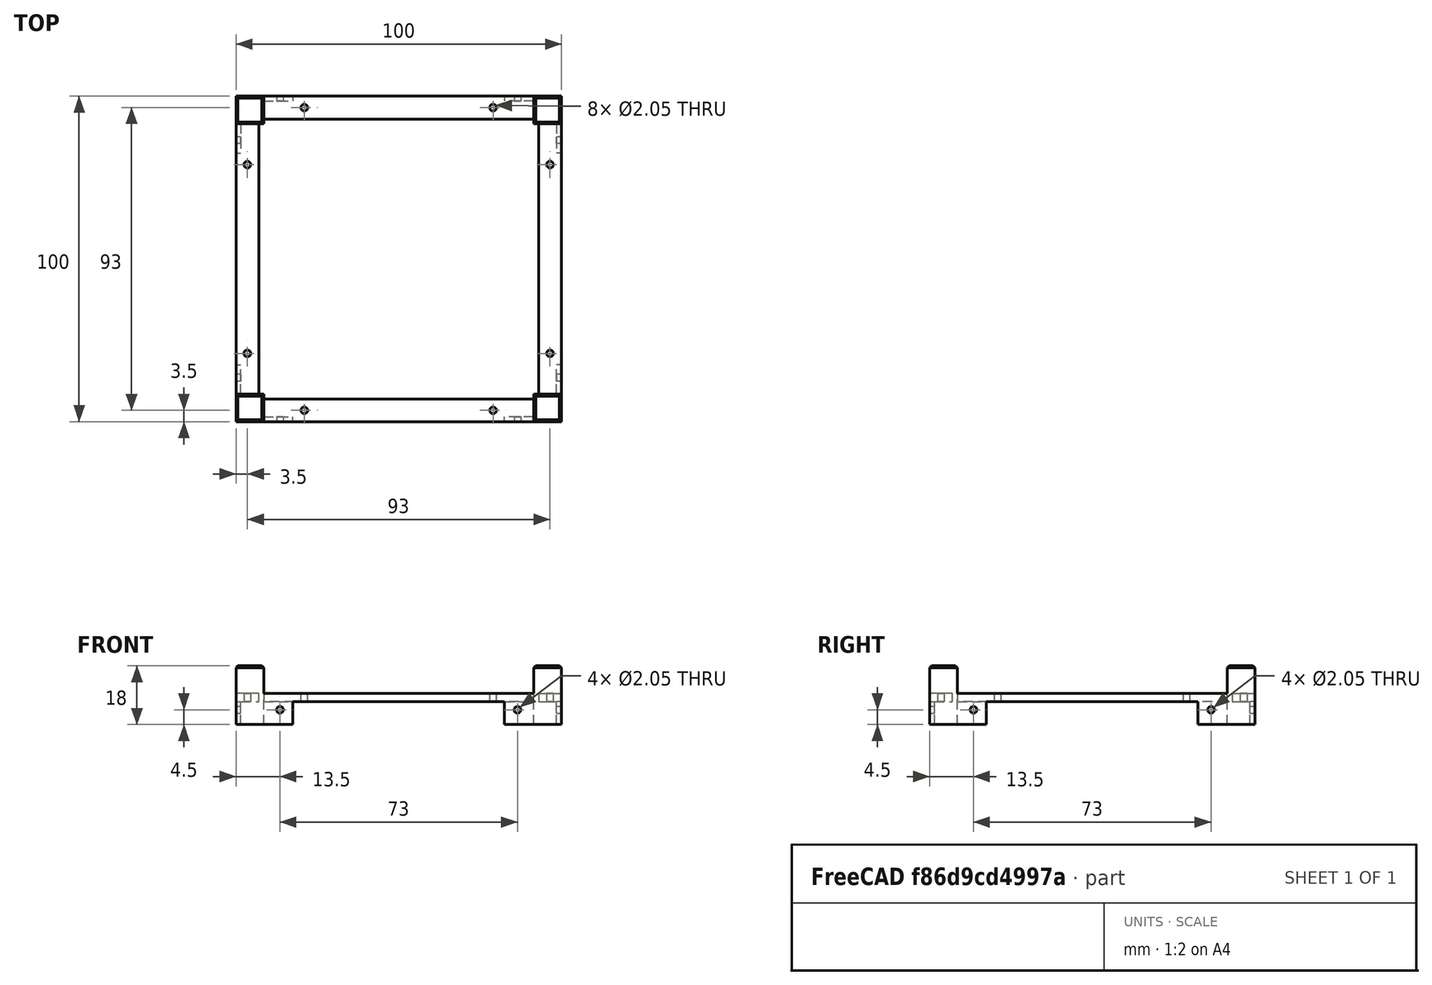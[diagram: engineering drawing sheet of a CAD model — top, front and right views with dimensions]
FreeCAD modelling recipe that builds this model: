
FCSTD DOCUMENT  (FreeCAD 0.20R29603 (Git))
Label: OpenSCAD_MyChassisModeling
License: All rights reserved
LicenseURL: http://en.wikipedia.org/wiki/All_rights_reserved
objects: Part::Box×72, Part::Fuse×56, Part::Cylinder×32, Part::Cut×17, Part::MultiFuse×13, Part::Mirroring×8, TechDraw::DrawViewDimension×5, TechDraw::DrawViewPart×3, Part::FeaturePython×1, TechDraw::DrawSVGTemplate×1, TechDraw::DrawViewAnnotation×1, TechDraw::DrawPage×1
note: 199 computed .brp shape members not serialized (recipe doc carries the construction recipe); baked Part::Feature solids carry a one-line shape summary decoded from their .brp

FEATURE [Part::Box] cube
  AttacherType = Attacher::AttachEngine3D
  Height = 2.5
  Length = 100
  Placement = pos=(-50,-3.5,-2.5) rot=(0,0,1;0rad)
  Width = 7
FEATURE [Part::Cylinder] cylinder
  Angle = 360
  AttacherType = Attacher::AttachEngine3D
  FirstAngle = 0
  Height = 100
  Placement = pos=(-29,0,-50) rot=(0,0,1;0rad)
  Radius = 1.025
  SecondAngle = 0
FEATURE [Part::Cylinder] cylinder001
  Angle = 360
  AttacherType = Attacher::AttachEngine3D
  FirstAngle = 0
  Height = 100
  Placement = pos=(29,0,-50) rot=(0,0,1;0rad)
  Radius = 1.025
  SecondAngle = 0
FEATURE [Part::Fuse] Group
  Base = -> cylinder
  Tool = -> cylinder001
FEATURE [Part::Cut] difference
  Base = -> cube
  Placement = pos=(0,46.5,0) rot=(0,0,1;0rad)
  Tool = -> Group
FEATURE [Part::Box] cube001
  AttacherType = Attacher::AttachEngine3D
  Height = 2.5
  Length = 100
  Placement = pos=(-50,-3.5,-2.5) rot=(0,0,1;0rad)
  Width = 7
FEATURE [Part::Cylinder] cylinder002
  Angle = 360
  AttacherType = Attacher::AttachEngine3D
  FirstAngle = 0
  Height = 100
  Placement = pos=(-29,0,-50) rot=(0,0,1;0rad)
  Radius = 1.025
  SecondAngle = 0
FEATURE [Part::Cylinder] cylinder003
  Angle = 360
  AttacherType = Attacher::AttachEngine3D
  FirstAngle = 0
  Height = 100
  Placement = pos=(29,0,-50) rot=(0,0,1;0rad)
  Radius = 1.025
  SecondAngle = 0
FEATURE [Part::Fuse] Group001
  Base = -> cylinder002
  Tool = -> cylinder003
FEATURE [Part::Cut] difference001
  Base = -> cube001
  Placement = pos=(0,46.5,0) rot=(0,0,1;0rad)
  Tool = -> Group001
FEATURE [Part::Fuse] Group002
  Base = -> difference
  Tool = -> difference001
FEATURE [Part::Box] cube002
  AttacherType = Attacher::AttachEngine3D
  Height = 2.5
  Length = 100
  Placement = pos=(-50,-3.5,-2.5) rot=(0,0,1;0rad)
  Width = 7
FEATURE [Part::Cylinder] cylinder004
  Angle = 360
  AttacherType = Attacher::AttachEngine3D
  FirstAngle = 0
  Height = 100
  Placement = pos=(-29,0,-50) rot=(0,0,1;0rad)
  Radius = 1.025
  SecondAngle = 0
FEATURE [Part::Cylinder] cylinder005
  Angle = 360
  AttacherType = Attacher::AttachEngine3D
  FirstAngle = 0
  Height = 100
  Placement = pos=(29,0,-50) rot=(0,0,1;0rad)
  Radius = 1.025
  SecondAngle = 0
FEATURE [Part::Fuse] Group003
  Base = -> cylinder004
  Tool = -> cylinder005
FEATURE [Part::Cut] difference002
  Base = -> cube002
  Placement = pos=(0,46.5,0) rot=(0,0,1;0rad)
  Tool = -> Group003
FEATURE [Part::Box] cube003
  AttacherType = Attacher::AttachEngine3D
  Height = 2.5
  Length = 100
  Placement = pos=(-50,-3.5,-2.5) rot=(0,0,1;0rad)
  Width = 7
FEATURE [Part::Cylinder] cylinder006
  Angle = 360
  AttacherType = Attacher::AttachEngine3D
  FirstAngle = 0
  Height = 100
  Placement = pos=(-29,0,-50) rot=(0,0,1;0rad)
  Radius = 1.025
  SecondAngle = 0
FEATURE [Part::Cylinder] cylinder007
  Angle = 360
  AttacherType = Attacher::AttachEngine3D
  FirstAngle = 0
  Height = 100
  Placement = pos=(29,0,-50) rot=(0,0,1;0rad)
  Radius = 1.025
  SecondAngle = 0
FEATURE [Part::Fuse] Group004
  Base = -> cylinder006
  Tool = -> cylinder007
FEATURE [Part::Cut] difference003
  Base = -> cube003
  Placement = pos=(-46.5,0,0) rot=(0,0,1;1.5708rad)
  Tool = -> Group004
FEATURE [Part::Fuse] Group005
  Base = -> difference002
  Tool = -> difference003
FEATURE [Part::Box] cube004
  AttacherType = Attacher::AttachEngine3D
  Height = 2.5
  Length = 100
  Placement = pos=(-50,-3.5,-2.5) rot=(0,0,1;0rad)
  Width = 7
FEATURE [Part::Cylinder] cylinder008
  Angle = 360
  AttacherType = Attacher::AttachEngine3D
  FirstAngle = 0
  Height = 100
  Placement = pos=(-29,0,-50) rot=(0,0,1;0rad)
  Radius = 1.025
  SecondAngle = 0
FEATURE [Part::Cylinder] cylinder009
  Angle = 360
  AttacherType = Attacher::AttachEngine3D
  FirstAngle = 0
  Height = 100
  Placement = pos=(29,0,-50) rot=(0,0,1;0rad)
  Radius = 1.025
  SecondAngle = 0
FEATURE [Part::Fuse] Group006
  Base = -> cylinder008
  Tool = -> cylinder009
FEATURE [Part::Cut] difference004
  Base = -> cube004
  Placement = pos=(0,46.5,0) rot=(0,0,1;0rad)
  Tool = -> Group006
FEATURE [Part::Box] cube005
  AttacherType = Attacher::AttachEngine3D
  Height = 2.5
  Length = 100
  Placement = pos=(-50,-3.5,-2.5) rot=(0,0,1;0rad)
  Width = 7
FEATURE [Part::Cylinder] cylinder010
  Angle = 360
  AttacherType = Attacher::AttachEngine3D
  FirstAngle = 0
  Height = 100
  Placement = pos=(-29,0,-50) rot=(0,0,1;0rad)
  Radius = 1.025
  SecondAngle = 0
FEATURE [Part::Cylinder] cylinder011
  Angle = 360
  AttacherType = Attacher::AttachEngine3D
  FirstAngle = 0
  Height = 100
  Placement = pos=(29,0,-50) rot=(0,0,1;0rad)
  Radius = 1.025
  SecondAngle = 0
FEATURE [Part::Fuse] Group007
  Base = -> cylinder010
  Tool = -> cylinder011
FEATURE [Part::Cut] difference005
  Base = -> cube005
  Placement = pos=(-5.7e-15,-46.5,0) rot=(0,0,1;3.14159rad)
  Tool = -> Group007
FEATURE [Part::Fuse] Group008
  Base = -> difference004
  Tool = -> difference005
FEATURE [Part::Box] cube006
  AttacherType = Attacher::AttachEngine3D
  Height = 2.5
  Length = 100
  Placement = pos=(-50,-3.5,-2.5) rot=(0,0,1;0rad)
  Width = 7
FEATURE [Part::Cylinder] cylinder012
  Angle = 360
  AttacherType = Attacher::AttachEngine3D
  FirstAngle = 0
  Height = 100
  Placement = pos=(-29,0,-50) rot=(0,0,1;0rad)
  Radius = 1.025
  SecondAngle = 0
FEATURE [Part::Cylinder] cylinder013
  Angle = 360
  AttacherType = Attacher::AttachEngine3D
  FirstAngle = 0
  Height = 100
  Placement = pos=(29,0,-50) rot=(0,0,1;0rad)
  Radius = 1.025
  SecondAngle = 0
FEATURE [Part::Fuse] Group009
  Base = -> cylinder012
  Tool = -> cylinder013
FEATURE [Part::Cut] difference006
  Base = -> cube006
  Placement = pos=(0,46.5,0) rot=(0,0,1;0rad)
  Tool = -> Group009
FEATURE [Part::Box] cube007
  AttacherType = Attacher::AttachEngine3D
  Height = 2.5
  Length = 100
  Placement = pos=(-50,-3.5,-2.5) rot=(0,0,1;0rad)
  Width = 7
FEATURE [Part::Cylinder] cylinder014
  Angle = 360
  AttacherType = Attacher::AttachEngine3D
  FirstAngle = 0
  Height = 100
  Placement = pos=(-29,0,-50) rot=(0,0,1;0rad)
  Radius = 1.025
  SecondAngle = 0
FEATURE [Part::Cylinder] cylinder015
  Angle = 360
  AttacherType = Attacher::AttachEngine3D
  FirstAngle = 0
  Height = 100
  Placement = pos=(29,0,-50) rot=(0,0,1;0rad)
  Radius = 1.025
  SecondAngle = 0
FEATURE [Part::Fuse] Group010
  Base = -> cylinder014
  Tool = -> cylinder015
FEATURE [Part::Cut] difference007
  Base = -> cube007
  Placement = pos=(46.5,0,0) rot=(0,0,-1;1.5708rad)
  Tool = -> Group010
FEATURE [Part::Fuse] Group011
  Base = -> difference006
  Tool = -> difference007
FEATURE [Part::MultiFuse] Group012
  Shapes = -> [Group002,Group005,Group008,Group011]
FEATURE [Part::Box] cube008
  AttacherType = Attacher::AttachEngine3D
  Height = 18
  Length = 8.5
  Placement = pos=(-4.25,-4.25,-18) rot=(0,0,1;0rad)
  Width = 8.5
FEATURE [Part::Box] cube009
  AttacherType = Attacher::AttachEngine3D
  Height = 100
  Length = 9.5
  Placement = pos=(-4.75,42.3466,-38.7141) rot=(1,0,0;0.785398rad)
  Width = 9.5
FEATURE [Part::Box] cube010
  AttacherType = Attacher::AttachEngine3D
  Height = 100
  Length = 9.5
  Placement = pos=(-42.3466,-4.75,-38.7141) rot=(0.357407,0.357407,0.862856;1.71777rad)
  Width = 9.5
FEATURE [Part::Fuse] Group013
  Base = -> cube009
  Tool = -> cube010
FEATURE [Part::Box] cube011
  AttacherType = Attacher::AttachEngine3D
  Height = 100
  Length = 9.5
  Placement = pos=(-4.75,42.3466,-38.7141) rot=(1,0,0;0.785398rad)
  Width = 9.5
FEATURE [Part::Box] cube012
  AttacherType = Attacher::AttachEngine3D
  Height = 100
  Length = 9.5
  Placement = pos=(4.75,-42.3466,-38.7141) rot=(0,0.382683,0.92388;3.14159rad)
  Width = 9.5
FEATURE [Part::Fuse] Group014
  Base = -> cube011
  Tool = -> cube012
FEATURE [Part::Box] cube013
  AttacherType = Attacher::AttachEngine3D
  Height = 100
  Length = 9.5
  Placement = pos=(-4.75,42.3466,-38.7141) rot=(1,0,0;0.785398rad)
  Width = 9.5
FEATURE [Part::Box] cube014
  AttacherType = Attacher::AttachEngine3D
  Height = 100
  Length = 9.5
  Placement = pos=(42.3466,4.75,-38.7141) rot=(0.357407,-0.357407,-0.862856;1.71777rad)
  Width = 9.5
FEATURE [Part::Fuse] Group015
  Base = -> cube013
  Tool = -> cube014
FEATURE [Part::MultiFuse] Group016
  Shapes = -> [Group013,Group014,Group015]
FEATURE [Part::Cut] difference008
  Base = -> cube008
  Placement = pos=(-45.75,-45.75,8.5) rot=(0,0,1;0rad)
  Tool = -> Group016
FEATURE [Part::Box] cube015
  AttacherType = Attacher::AttachEngine3D
  Height = 18
  Length = 8.5
  Placement = pos=(-4.25,-4.25,-18) rot=(0,0,1;0rad)
  Width = 8.5
FEATURE [Part::Box] cube016
  AttacherType = Attacher::AttachEngine3D
  Height = 100
  Length = 9.5
  Placement = pos=(-4.75,42.3466,-38.7141) rot=(1,0,0;0.785398rad)
  Width = 9.5
FEATURE [Part::Box] cube017
  AttacherType = Attacher::AttachEngine3D
  Height = 100
  Length = 9.5
  Placement = pos=(-42.3466,-4.75,-38.7141) rot=(0.357407,0.357407,0.862856;1.71777rad)
  Width = 9.5
FEATURE [Part::Fuse] Group017
  Base = -> cube016
  Tool = -> cube017
FEATURE [Part::Box] cube018
  AttacherType = Attacher::AttachEngine3D
  Height = 100
  Length = 9.5
  Placement = pos=(-4.75,42.3466,-38.7141) rot=(1,0,0;0.785398rad)
  Width = 9.5
FEATURE [Part::Box] cube019
  AttacherType = Attacher::AttachEngine3D
  Height = 100
  Length = 9.5
  Placement = pos=(4.75,-42.3466,-38.7141) rot=(0,0.382683,0.92388;3.14159rad)
  Width = 9.5
FEATURE [Part::Fuse] Group018
  Base = -> cube018
  Tool = -> cube019
FEATURE [Part::Box] cube020
  AttacherType = Attacher::AttachEngine3D
  Height = 100
  Length = 9.5
  Placement = pos=(-4.75,42.3466,-38.7141) rot=(1,0,0;0.785398rad)
  Width = 9.5
FEATURE [Part::Box] cube021
  AttacherType = Attacher::AttachEngine3D
  Height = 100
  Length = 9.5
  Placement = pos=(42.3466,4.75,-38.7141) rot=(0.357407,-0.357407,-0.862856;1.71777rad)
  Width = 9.5
FEATURE [Part::Fuse] Group019
  Base = -> cube020
  Tool = -> cube021
FEATURE [Part::MultiFuse] Group020
  Shapes = -> [Group017,Group018,Group019]
FEATURE [Part::Cut] difference009
  Base = -> cube015
  Placement = pos=(-45.75,-45.75,8.5) rot=(0,0,1;0rad)
  Tool = -> Group020
FEATURE [Part::Fuse] Group021
  Base = -> difference008
  Tool = -> difference009
FEATURE [Part::Box] cube022
  AttacherType = Attacher::AttachEngine3D
  Height = 18
  Length = 8.5
  Placement = pos=(-4.25,-4.25,-18) rot=(0,0,1;0rad)
  Width = 8.5
FEATURE [Part::Box] cube023
  AttacherType = Attacher::AttachEngine3D
  Height = 100
  Length = 9.5
  Placement = pos=(-4.75,42.3466,-38.7141) rot=(1,0,0;0.785398rad)
  Width = 9.5
FEATURE [Part::Box] cube024
  AttacherType = Attacher::AttachEngine3D
  Height = 100
  Length = 9.5
  Placement = pos=(-42.3466,-4.75,-38.7141) rot=(0.357407,0.357407,0.862856;1.71777rad)
  Width = 9.5
FEATURE [Part::Fuse] Group022
  Base = -> cube023
  Tool = -> cube024
FEATURE [Part::Box] cube025
  AttacherType = Attacher::AttachEngine3D
  Height = 100
  Length = 9.5
  Placement = pos=(-4.75,42.3466,-38.7141) rot=(1,0,0;0.785398rad)
  Width = 9.5
FEATURE [Part::Box] cube026
  AttacherType = Attacher::AttachEngine3D
  Height = 100
  Length = 9.5
  Placement = pos=(4.75,-42.3466,-38.7141) rot=(0,0.382683,0.92388;3.14159rad)
  Width = 9.5
FEATURE [Part::Fuse] Group023
  Base = -> cube025
  Tool = -> cube026
FEATURE [Part::Box] cube027
  AttacherType = Attacher::AttachEngine3D
  Height = 100
  Length = 9.5
  Placement = pos=(-4.75,42.3466,-38.7141) rot=(1,0,0;0.785398rad)
  Width = 9.5
FEATURE [Part::Box] cube028
  AttacherType = Attacher::AttachEngine3D
  Height = 100
  Length = 9.5
  Placement = pos=(42.3466,4.75,-38.7141) rot=(0.357407,-0.357407,-0.862856;1.71777rad)
  Width = 9.5
FEATURE [Part::Fuse] Group024
  Base = -> cube027
  Tool = -> cube028
FEATURE [Part::MultiFuse] Group025
  Shapes = -> [Group022,Group023,Group024]
FEATURE [Part::Cut] difference010
  Base = -> cube022
  Placement = pos=(-45.75,-45.75,8.5) rot=(0,0,1;0rad)
  Tool = -> Group025
FEATURE [Part::Box] cube029
  AttacherType = Attacher::AttachEngine3D
  Height = 18
  Length = 8.5
  Placement = pos=(-4.25,-4.25,-18) rot=(0,0,1;0rad)
  Width = 8.5
FEATURE [Part::Box] cube030
  AttacherType = Attacher::AttachEngine3D
  Height = 100
  Length = 9.5
  Placement = pos=(-4.75,42.3466,-38.7141) rot=(1,0,0;0.785398rad)
  Width = 9.5
FEATURE [Part::Box] cube031
  AttacherType = Attacher::AttachEngine3D
  Height = 100
  Length = 9.5
  Placement = pos=(-42.3466,-4.75,-38.7141) rot=(0.357407,0.357407,0.862856;1.71777rad)
  Width = 9.5
FEATURE [Part::Fuse] Group026
  Base = -> cube030
  Tool = -> cube031
FEATURE [Part::Box] cube032
  AttacherType = Attacher::AttachEngine3D
  Height = 100
  Length = 9.5
  Placement = pos=(-4.75,42.3466,-38.7141) rot=(1,0,0;0.785398rad)
  Width = 9.5
FEATURE [Part::Box] cube033
  AttacherType = Attacher::AttachEngine3D
  Height = 100
  Length = 9.5
  Placement = pos=(4.75,-42.3466,-38.7141) rot=(0,0.382683,0.92388;3.14159rad)
  Width = 9.5
FEATURE [Part::Fuse] Group027
  Base = -> cube032
  Tool = -> cube033
FEATURE [Part::Box] cube034
  AttacherType = Attacher::AttachEngine3D
  Height = 100
  Length = 9.5
  Placement = pos=(-4.75,42.3466,-38.7141) rot=(1,0,0;0.785398rad)
  Width = 9.5
FEATURE [Part::Box] cube035
  AttacherType = Attacher::AttachEngine3D
  Height = 100
  Length = 9.5
  Placement = pos=(42.3466,4.75,-38.7141) rot=(0.357407,-0.357407,-0.862856;1.71777rad)
  Width = 9.5
FEATURE [Part::Fuse] Group028
  Base = -> cube034
  Tool = -> cube035
FEATURE [Part::MultiFuse] Group029
  Shapes = -> [Group026,Group027,Group028]
FEATURE [Part::Cut] difference011
  Base = -> cube029
  Placement = pos=(45.75,-45.75,8.5) rot=(0,0,1;1.5708rad)
  Tool = -> Group029
FEATURE [Part::Fuse] Group030
  Base = -> difference010
  Tool = -> difference011
FEATURE [Part::Box] cube036
  AttacherType = Attacher::AttachEngine3D
  Height = 18
  Length = 8.5
  Placement = pos=(-4.25,-4.25,-18) rot=(0,0,1;0rad)
  Width = 8.5
FEATURE [Part::Box] cube037
  AttacherType = Attacher::AttachEngine3D
  Height = 100
  Length = 9.5
  Placement = pos=(-4.75,42.3466,-38.7141) rot=(1,0,0;0.785398rad)
  Width = 9.5
FEATURE [Part::Box] cube038
  AttacherType = Attacher::AttachEngine3D
  Height = 100
  Length = 9.5
  Placement = pos=(-42.3466,-4.75,-38.7141) rot=(0.357407,0.357407,0.862856;1.71777rad)
  Width = 9.5
FEATURE [Part::Fuse] Group031
  Base = -> cube037
  Tool = -> cube038
FEATURE [Part::Box] cube039
  AttacherType = Attacher::AttachEngine3D
  Height = 100
  Length = 9.5
  Placement = pos=(-4.75,42.3466,-38.7141) rot=(1,0,0;0.785398rad)
  Width = 9.5
FEATURE [Part::Box] cube040
  AttacherType = Attacher::AttachEngine3D
  Height = 100
  Length = 9.5
  Placement = pos=(4.75,-42.3466,-38.7141) rot=(0,0.382683,0.92388;3.14159rad)
  Width = 9.5
FEATURE [Part::Fuse] Group032
  Base = -> cube039
  Tool = -> cube040
FEATURE [Part::Box] cube041
  AttacherType = Attacher::AttachEngine3D
  Height = 100
  Length = 9.5
  Placement = pos=(-4.75,42.3466,-38.7141) rot=(1,0,0;0.785398rad)
  Width = 9.5
FEATURE [Part::Box] cube042
  AttacherType = Attacher::AttachEngine3D
  Height = 100
  Length = 9.5
  Placement = pos=(42.3466,4.75,-38.7141) rot=(0.357407,-0.357407,-0.862856;1.71777rad)
  Width = 9.5
FEATURE [Part::Fuse] Group033
  Base = -> cube041
  Tool = -> cube042
FEATURE [Part::MultiFuse] Group034
  Shapes = -> [Group031,Group032,Group033]
FEATURE [Part::Cut] difference012
  Base = -> cube036
  Placement = pos=(-45.75,-45.75,8.5) rot=(0,0,1;0rad)
  Tool = -> Group034
FEATURE [Part::Box] cube043
  AttacherType = Attacher::AttachEngine3D
  Height = 18
  Length = 8.5
  Placement = pos=(-4.25,-4.25,-18) rot=(0,0,1;0rad)
  Width = 8.5
FEATURE [Part::Box] cube044
  AttacherType = Attacher::AttachEngine3D
  Height = 100
  Length = 9.5
  Placement = pos=(-4.75,42.3466,-38.7141) rot=(1,0,0;0.785398rad)
  Width = 9.5
FEATURE [Part::Box] cube045
  AttacherType = Attacher::AttachEngine3D
  Height = 100
  Length = 9.5
  Placement = pos=(-42.3466,-4.75,-38.7141) rot=(0.357407,0.357407,0.862856;1.71777rad)
  Width = 9.5
FEATURE [Part::Fuse] Group035
  Base = -> cube044
  Tool = -> cube045
FEATURE [Part::Box] cube046
  AttacherType = Attacher::AttachEngine3D
  Height = 100
  Length = 9.5
  Placement = pos=(-4.75,42.3466,-38.7141) rot=(1,0,0;0.785398rad)
  Width = 9.5
FEATURE [Part::Box] cube047
  AttacherType = Attacher::AttachEngine3D
  Height = 100
  Length = 9.5
  Placement = pos=(4.75,-42.3466,-38.7141) rot=(0,0.382683,0.92388;3.14159rad)
  Width = 9.5
FEATURE [Part::Fuse] Group036
  Base = -> cube046
  Tool = -> cube047
FEATURE [Part::Box] cube048
  AttacherType = Attacher::AttachEngine3D
  Height = 100
  Length = 9.5
  Placement = pos=(-4.75,42.3466,-38.7141) rot=(1,0,0;0.785398rad)
  Width = 9.5
FEATURE [Part::Box] cube049
  AttacherType = Attacher::AttachEngine3D
  Height = 100
  Length = 9.5
  Placement = pos=(42.3466,4.75,-38.7141) rot=(0.357407,-0.357407,-0.862856;1.71777rad)
  Width = 9.5
FEATURE [Part::Fuse] Group037
  Base = -> cube048
  Tool = -> cube049
FEATURE [Part::MultiFuse] Group038
  Shapes = -> [Group035,Group036,Group037]
FEATURE [Part::Cut] difference013
  Base = -> cube043
  Placement = pos=(45.75,45.75,8.5) rot=(0,0,1;3.14159rad)
  Tool = -> Group038
FEATURE [Part::Fuse] Group039
  Base = -> difference012
  Tool = -> difference013
FEATURE [Part::Box] cube050
  AttacherType = Attacher::AttachEngine3D
  Height = 18
  Length = 8.5
  Placement = pos=(-4.25,-4.25,-18) rot=(0,0,1;0rad)
  Width = 8.5
FEATURE [Part::Box] cube051
  AttacherType = Attacher::AttachEngine3D
  Height = 100
  Length = 9.5
  Placement = pos=(-4.75,42.3466,-38.7141) rot=(1,0,0;0.785398rad)
  Width = 9.5
FEATURE [Part::Box] cube052
  AttacherType = Attacher::AttachEngine3D
  Height = 100
  Length = 9.5
  Placement = pos=(-42.3466,-4.75,-38.7141) rot=(0.357407,0.357407,0.862856;1.71777rad)
  Width = 9.5
FEATURE [Part::Fuse] Group040
  Base = -> cube051
  Tool = -> cube052
FEATURE [Part::Box] cube053
  AttacherType = Attacher::AttachEngine3D
  Height = 100
  Length = 9.5
  Placement = pos=(-4.75,42.3466,-38.7141) rot=(1,0,0;0.785398rad)
  Width = 9.5
FEATURE [Part::Box] cube054
  AttacherType = Attacher::AttachEngine3D
  Height = 100
  Length = 9.5
  Placement = pos=(4.75,-42.3466,-38.7141) rot=(0,0.382683,0.92388;3.14159rad)
  Width = 9.5
FEATURE [Part::Fuse] Group041
  Base = -> cube053
  Tool = -> cube054
FEATURE [Part::Box] cube055
  AttacherType = Attacher::AttachEngine3D
  Height = 100
  Length = 9.5
  Placement = pos=(-4.75,42.3466,-38.7141) rot=(1,0,0;0.785398rad)
  Width = 9.5
FEATURE [Part::Box] cube056
  AttacherType = Attacher::AttachEngine3D
  Height = 100
  Length = 9.5
  Placement = pos=(42.3466,4.75,-38.7141) rot=(0.357407,-0.357407,-0.862856;1.71777rad)
  Width = 9.5
FEATURE [Part::Fuse] Group042
  Base = -> cube055
  Tool = -> cube056
FEATURE [Part::MultiFuse] Group043
  Shapes = -> [Group040,Group041,Group042]
FEATURE [Part::Cut] difference014
  Base = -> cube050
  Placement = pos=(-45.75,-45.75,8.5) rot=(0,0,1;0rad)
  Tool = -> Group043
FEATURE [Part::Box] cube057
  AttacherType = Attacher::AttachEngine3D
  Height = 18
  Length = 8.5
  Placement = pos=(-4.25,-4.25,-18) rot=(0,0,1;0rad)
  Width = 8.5
FEATURE [Part::Box] cube058
  AttacherType = Attacher::AttachEngine3D
  Height = 100
  Length = 9.5
  Placement = pos=(-4.75,42.3466,-38.7141) rot=(1,0,0;0.785398rad)
  Width = 9.5
FEATURE [Part::Box] cube059
  AttacherType = Attacher::AttachEngine3D
  Height = 100
  Length = 9.5
  Placement = pos=(-42.3466,-4.75,-38.7141) rot=(0.357407,0.357407,0.862856;1.71777rad)
  Width = 9.5
FEATURE [Part::Fuse] Group044
  Base = -> cube058
  Tool = -> cube059
FEATURE [Part::Box] cube060
  AttacherType = Attacher::AttachEngine3D
  Height = 100
  Length = 9.5
  Placement = pos=(-4.75,42.3466,-38.7141) rot=(1,0,0;0.785398rad)
  Width = 9.5
FEATURE [Part::Box] cube061
  AttacherType = Attacher::AttachEngine3D
  Height = 100
  Length = 9.5
  Placement = pos=(4.75,-42.3466,-38.7141) rot=(0,0.382683,0.92388;3.14159rad)
  Width = 9.5
FEATURE [Part::Fuse] Group045
  Base = -> cube060
  Tool = -> cube061
FEATURE [Part::Box] cube062
  AttacherType = Attacher::AttachEngine3D
  Height = 100
  Length = 9.5
  Placement = pos=(-4.75,42.3466,-38.7141) rot=(1,0,0;0.785398rad)
  Width = 9.5
FEATURE [Part::Box] cube063
  AttacherType = Attacher::AttachEngine3D
  Height = 100
  Length = 9.5
  Placement = pos=(42.3466,4.75,-38.7141) rot=(0.357407,-0.357407,-0.862856;1.71777rad)
  Width = 9.5
FEATURE [Part::Fuse] Group046
  Base = -> cube062
  Tool = -> cube063
FEATURE [Part::MultiFuse] Group047
  Shapes = -> [Group044,Group045,Group046]
FEATURE [Part::Cut] difference015
  Base = -> cube057
  Placement = pos=(-45.75,45.75,8.5) rot=(0,0,-1;1.5708rad)
  Tool = -> Group047
FEATURE [Part::Fuse] Group048
  Base = -> difference014
  Tool = -> difference015
FEATURE [Part::MultiFuse] Group049
  Shapes = -> [Group021,Group030,Group039,Group048]
FEATURE [Part::Box] cube064
  AttacherType = Attacher::AttachEngine3D
  Height = 9.5
  Length = 1.5
  Placement = pos=(48.5,-41.5,-9.5) rot=(0,0,1;0rad)
  Width = 9
FEATURE [Part::Box] cube065
  AttacherType = Attacher::AttachEngine3D
  Height = 9.5
  Length = 1.5
  Placement = pos=(48.5,-41.5,-9.5) rot=(0,0,1;0rad)
  Width = 9
FEATURE [Part::Mirroring] mirr_cube065  label="mirrored cube065"
  Base = (0,0,0)
  Normal = (0,1,0)
  Source = -> cube065
FEATURE [Part::Fuse] Group050
  Base = -> cube064
  Tool = -> mirr_cube065
FEATURE [Part::Box] cube066
  AttacherType = Attacher::AttachEngine3D
  Height = 9.5
  Length = 1.5
  Placement = pos=(48.5,-41.5,-9.5) rot=(0,0,1;0rad)
  Width = 9
FEATURE [Part::Box] cube067
  AttacherType = Attacher::AttachEngine3D
  Height = 9.5
  Length = 1.5
  Placement = pos=(48.5,-41.5,-9.5) rot=(0,0,1;0rad)
  Width = 9
FEATURE [Part::Mirroring] mirr_cube067  label="mirrored cube067"
  Base = (0,0,0)
  Normal = (0,1,0)
  Source = -> cube067
FEATURE [Part::Fuse] Group051
  Base = -> cube066
  Placement = pos=(0,0,0) rot=(0,0,1;1.5708rad)
  Tool = -> mirr_cube067
FEATURE [Part::Box] cube068
  AttacherType = Attacher::AttachEngine3D
  Height = 9.5
  Length = 1.5
  Placement = pos=(48.5,-41.5,-9.5) rot=(0,0,1;0rad)
  Width = 9
FEATURE [Part::Box] cube069
  AttacherType = Attacher::AttachEngine3D
  Height = 9.5
  Length = 1.5
  Placement = pos=(48.5,-41.5,-9.5) rot=(0,0,1;0rad)
  Width = 9
FEATURE [Part::Mirroring] mirr_cube069  label="mirrored cube069"
  Base = (0,0,0)
  Normal = (0,1,0)
  Source = -> cube069
FEATURE [Part::Fuse] Group052
  Base = -> cube068
  Placement = pos=(0,0,0) rot=(0,0,1;3.14159rad)
  Tool = -> mirr_cube069
FEATURE [Part::Box] cube070
  AttacherType = Attacher::AttachEngine3D
  Height = 9.5
  Length = 1.5
  Placement = pos=(48.5,-41.5,-9.5) rot=(0,0,1;0rad)
  Width = 9
FEATURE [Part::Box] cube071
  AttacherType = Attacher::AttachEngine3D
  Height = 9.5
  Length = 1.5
  Placement = pos=(48.5,-41.5,-9.5) rot=(0,0,1;0rad)
  Width = 9
FEATURE [Part::Mirroring] mirr_cube071  label="mirrored cube071"
  Base = (0,0,0)
  Normal = (0,1,0)
  Source = -> cube071
FEATURE [Part::Fuse] Group053
  Base = -> cube070
  Placement = pos=(0,0,0) rot=(0,0,-1;1.5708rad)
  Tool = -> mirr_cube071
FEATURE [Part::MultiFuse] Group054
  Shapes = -> [Group050,Group051,Group052,Group053]
FEATURE [Part::Cylinder] cylinder016
  Angle = 360
  AttacherType = Attacher::AttachEngine3D
  FirstAngle = 0
  Height = 500
  Placement = pos=(-250,-36.5,-5) rot=(0,1,0;1.5708rad)
  Radius = 1.025
  SecondAngle = 0
FEATURE [Part::Cylinder] cylinder017
  Angle = 360
  AttacherType = Attacher::AttachEngine3D
  FirstAngle = 0
  Height = 500
  Placement = pos=(-250,-29,-5) rot=(0,1,0;1.5708rad)
  Radius = 1.025
  SecondAngle = 0
FEATURE [Part::Fuse] Group055
  Base = -> cylinder016
  Tool = -> cylinder017
FEATURE [Part::Cylinder] cylinder018
  Angle = 360
  AttacherType = Attacher::AttachEngine3D
  FirstAngle = 0
  Height = 500
  Placement = pos=(-250,-36.5,-5) rot=(0,1,0;1.5708rad)
  Radius = 1.025
  SecondAngle = 0
FEATURE [Part::Cylinder] cylinder019
  Angle = 360
  AttacherType = Attacher::AttachEngine3D
  FirstAngle = 0
  Height = 500
  Placement = pos=(-250,-29,-5) rot=(0,1,0;1.5708rad)
  Radius = 1.025
  SecondAngle = 0
FEATURE [Part::Fuse] Group056
  Base = -> cylinder018
  Tool = -> cylinder019
FEATURE [Part::Mirroring] mirr_Group056  label="mirrored Group056"
  Base = (0,0,0)
  Normal = (0,1,0)
  Source = -> Group056
FEATURE [Part::Fuse] Group057
  Base = -> Group055
  Tool = -> mirr_Group056
FEATURE [Part::Cylinder] cylinder020
  Angle = 360
  AttacherType = Attacher::AttachEngine3D
  FirstAngle = 0
  Height = 500
  Placement = pos=(-250,-36.5,-5) rot=(0,1,0;1.5708rad)
  Radius = 1.025
  SecondAngle = 0
FEATURE [Part::Cylinder] cylinder021
  Angle = 360
  AttacherType = Attacher::AttachEngine3D
  FirstAngle = 0
  Height = 500
  Placement = pos=(-250,-29,-5) rot=(0,1,0;1.5708rad)
  Radius = 1.025
  SecondAngle = 0
FEATURE [Part::Fuse] Group058
  Base = -> cylinder020
  Tool = -> cylinder021
FEATURE [Part::Cylinder] cylinder022
  Angle = 360
  AttacherType = Attacher::AttachEngine3D
  FirstAngle = 0
  Height = 500
  Placement = pos=(-250,-36.5,-5) rot=(0,1,0;1.5708rad)
  Radius = 1.025
  SecondAngle = 0
FEATURE [Part::Cylinder] cylinder023
  Angle = 360
  AttacherType = Attacher::AttachEngine3D
  FirstAngle = 0
  Height = 500
  Placement = pos=(-250,-29,-5) rot=(0,1,0;1.5708rad)
  Radius = 1.025
  SecondAngle = 0
FEATURE [Part::Fuse] Group059
  Base = -> cylinder022
  Tool = -> cylinder023
FEATURE [Part::Mirroring] mirr_Group059  label="mirrored Group059"
  Base = (0,0,0)
  Normal = (0,1,0)
  Source = -> Group059
FEATURE [Part::Fuse] Group060
  Base = -> Group058
  Placement = pos=(0,0,0) rot=(0,0,1;1.5708rad)
  Tool = -> mirr_Group059
FEATURE [Part::Cylinder] cylinder024
  Angle = 360
  AttacherType = Attacher::AttachEngine3D
  FirstAngle = 0
  Height = 500
  Placement = pos=(-250,-36.5,-5) rot=(0,1,0;1.5708rad)
  Radius = 1.025
  SecondAngle = 0
FEATURE [Part::Cylinder] cylinder025
  Angle = 360
  AttacherType = Attacher::AttachEngine3D
  FirstAngle = 0
  Height = 500
  Placement = pos=(-250,-29,-5) rot=(0,1,0;1.5708rad)
  Radius = 1.025
  SecondAngle = 0
FEATURE [Part::Fuse] Group061
  Base = -> cylinder024
  Tool = -> cylinder025
FEATURE [Part::Cylinder] cylinder026
  Angle = 360
  AttacherType = Attacher::AttachEngine3D
  FirstAngle = 0
  Height = 500
  Placement = pos=(-250,-36.5,-5) rot=(0,1,0;1.5708rad)
  Radius = 1.025
  SecondAngle = 0
FEATURE [Part::Cylinder] cylinder027
  Angle = 360
  AttacherType = Attacher::AttachEngine3D
  FirstAngle = 0
  Height = 500
  Placement = pos=(-250,-29,-5) rot=(0,1,0;1.5708rad)
  Radius = 1.025
  SecondAngle = 0
FEATURE [Part::Fuse] Group062
  Base = -> cylinder026
  Tool = -> cylinder027
FEATURE [Part::Mirroring] mirr_Group062  label="mirrored Group062"
  Base = (0,0,0)
  Normal = (0,1,0)
  Source = -> Group062
FEATURE [Part::Fuse] Group063
  Base = -> Group061
  Placement = pos=(0,0,0) rot=(0,0,1;3.14159rad)
  Tool = -> mirr_Group062
FEATURE [Part::Cylinder] cylinder028
  Angle = 360
  AttacherType = Attacher::AttachEngine3D
  FirstAngle = 0
  Height = 500
  Placement = pos=(-250,-36.5,-5) rot=(0,1,0;1.5708rad)
  Radius = 1.025
  SecondAngle = 0
FEATURE [Part::Cylinder] cylinder029
  Angle = 360
  AttacherType = Attacher::AttachEngine3D
  FirstAngle = 0
  Height = 500
  Placement = pos=(-250,-29,-5) rot=(0,1,0;1.5708rad)
  Radius = 1.025
  SecondAngle = 0
FEATURE [Part::Fuse] Group064
  Base = -> cylinder028
  Tool = -> cylinder029
FEATURE [Part::Cylinder] cylinder030
  Angle = 360
  AttacherType = Attacher::AttachEngine3D
  FirstAngle = 0
  Height = 500
  Placement = pos=(-250,-36.5,-5) rot=(0,1,0;1.5708rad)
  Radius = 1.025
  SecondAngle = 0
FEATURE [Part::Cylinder] cylinder031
  Angle = 360
  AttacherType = Attacher::AttachEngine3D
  FirstAngle = 0
  Height = 500
  Placement = pos=(-250,-29,-5) rot=(0,1,0;1.5708rad)
  Radius = 1.025
  SecondAngle = 0
FEATURE [Part::Fuse] Group065
  Base = -> cylinder030
  Tool = -> cylinder031
FEATURE [Part::Mirroring] mirr_Group065  label="mirrored Group065"
  Base = (0,0,0)
  Normal = (0,1,0)
  Source = -> Group065
FEATURE [Part::Fuse] Group066
  Base = -> Group064
  Placement = pos=(0,0,0) rot=(0,0,-1;1.5708rad)
  Tool = -> mirr_Group065
FEATURE [Part::MultiFuse] Group067
  Shapes = -> [Group057,Group060,Group063,Group066]
FEATURE [Part::Cut] difference016
  Base = -> Group054
  Tool = -> Group067
FEATURE [Part::MultiFuse] union
  Shapes = -> [Group012,Group049,difference016]
FEATURE [Part::FeaturePython] refine  label="refine_union"  # WARN: FeaturePython — macro-defined, semantics opaque (R4)
  Base = -> union
FEATURE [TechDraw::DrawSVGTemplate] Template
  Height = 297
  Orientation = 1
  Width = 420
FEATURE [TechDraw::DrawViewPart] View  label="SideView"
  CoarseView = false
  Direction = (0,-1,0)
  Focus = 100
  HardHidden = false
  IsoCount = 0
  IsoHidden = false
  IsoVisible = false
  LockPosition = false
  Perspective = false
  Rotation = 0
  ScaleType = 0
  SeamHidden = false
  SeamVisible = true
  SmoothHidden = false
  SmoothVisible = true
  Source = -> [refine]
  X = 300.162
  XDirection = (1,0,0)
  Y = 104.599
FEATURE [TechDraw::DrawViewPart] View001  label="TopView"
  CoarseView = false
  Direction = (0,0,-1)
  Focus = 100
  HardHidden = false
  IsoCount = 0
  IsoHidden = false
  IsoVisible = false
  LockPosition = false
  Perspective = false
  Rotation = 0
  ScaleType = 0
  SeamHidden = false
  SeamVisible = true
  SmoothHidden = false
  SmoothVisible = true
  Source = -> [refine]
  X = 118.422
  XDirection = (1,0,0)
  Y = 195.705
FEATURE [TechDraw::DrawViewPart] View002
  CoarseView = false
  Direction = (-0.5,0.5,0.707)
  Focus = 100
  HardHidden = false
  IsoCount = 0
  IsoHidden = false
  IsoVisible = false
  LockPosition = false
  Perspective = false
  Rotation = 0
  ScaleType = 0
  SeamHidden = false
  SeamVisible = true
  SmoothHidden = false
  SmoothVisible = true
  Source = -> [refine]
  X = 297.802
  XDirection = (-0.707,-0.707,0)
  Y = 197.121
FEATURE [TechDraw::DrawViewAnnotation] Annotation
  Font = osifont
  LineSpace = 80
  LockPosition = false
  MaxWidth = -1
  Rotation = 0
  ScaleType = 0
  Text = Unit: Millimeters (mm) | - All holes are threaded for M2.5x0.45 screw | - Tolerance follow ISO 2768 standards | - NO retaining sharp corners required
  TextSize = 5
  TextStyle = 0
  X = 118.422
  Y = 98.9344
FEATURE [TechDraw::DrawViewDimension] Dimension
  AngleOverride = false
  Arbitrary = false
  ArbitraryTolerances = false
  EqualTolerance = true
  ExtensionAngle = 0
  FormatSpec = %.2w
  FormatSpecOverTolerance = %+.2w
  FormatSpecUnderTolerance = %+.2w
  Inverted = false
  LineAngle = 0
  LockPosition = false
  MeasureType = 1
  OverTolerance = 0
  References2D = -> [View001]
  Rotation = 0
  ScaleType = 0
  TheoreticalExact = false
  Type = 2
  UnderTolerance = 0
  X = -63.1126
  Y = 0.860927
FEATURE [TechDraw::DrawViewDimension] Dimension001
  AngleOverride = false
  Arbitrary = false
  ArbitraryTolerances = false
  EqualTolerance = true
  ExtensionAngle = 0
  FormatSpec = %.2w
  FormatSpecOverTolerance = %+.2w
  FormatSpecUnderTolerance = %+.2w
  Inverted = false
  LineAngle = 0
  LockPosition = false
  MeasureType = 1
  OverTolerance = 0
  References2D = -> [View001]
  Rotation = 0
  ScaleType = 0
  TheoreticalExact = false
  Type = 1
  UnderTolerance = 0
  X = -0.273179
  Y = 64.2467
FEATURE [TechDraw::DrawViewDimension] Dimension002
  AngleOverride = false
  Arbitrary = false
  ArbitraryTolerances = false
  EqualTolerance = true
  ExtensionAngle = 0
  FormatSpec = %.2w
  FormatSpecOverTolerance = %+.2w
  FormatSpecUnderTolerance = %+.2w
  Inverted = false
  LineAngle = 0
  LockPosition = false
  MeasureType = 1
  OverTolerance = 0
  References2D = -> [View]
  Rotation = 0
  ScaleType = 0
  TheoreticalExact = false
  Type = 2
  UnderTolerance = 0
  X = 59.6087
  Y = 1.97803
FEATURE [TechDraw::DrawViewDimension] Dimension003
  AngleOverride = false
  Arbitrary = false
  ArbitraryTolerances = false
  EqualTolerance = true
  ExtensionAngle = 0
  FormatSpec = ⌀%.2w
  FormatSpecOverTolerance = %+.2w
  FormatSpecUnderTolerance = %+.2w
  Inverted = false
  LineAngle = 0
  LockPosition = false
  MeasureType = 1
  OverTolerance = 0
  References2D = -> [View001]
  Rotation = 0
  ScaleType = 0
  TheoreticalExact = false
  Type = 5
  UnderTolerance = 0
  X = 65.2306
  Y = 34.6357
FEATURE [TechDraw::DrawViewDimension] Dimension004
  AngleOverride = false
  Arbitrary = false
  ArbitraryTolerances = false
  EqualTolerance = true
  ExtensionAngle = 0
  FormatSpec = ⌀%.2w
  FormatSpecOverTolerance = %+.2w
  FormatSpecUnderTolerance = %+.2w
  Inverted = false
  LineAngle = 0
  LockPosition = false
  MeasureType = 1
  OverTolerance = 0
  References2D = -> [View]
  Rotation = 0
  ScaleType = 0
  TheoreticalExact = false
  Type = 5
  UnderTolerance = 0
  X = -61.182
  Y = 0.889457
FEATURE [TechDraw::DrawPage] Page
  KeepUpdated = true
  NextBalloonIndex = 1
  ProjectionType = 0
  Template = -> Template
  Views = -> [View,View001,View002,Annotation,Dimension,Dimension001,Dimension002,Dimension003,Dimension004]
